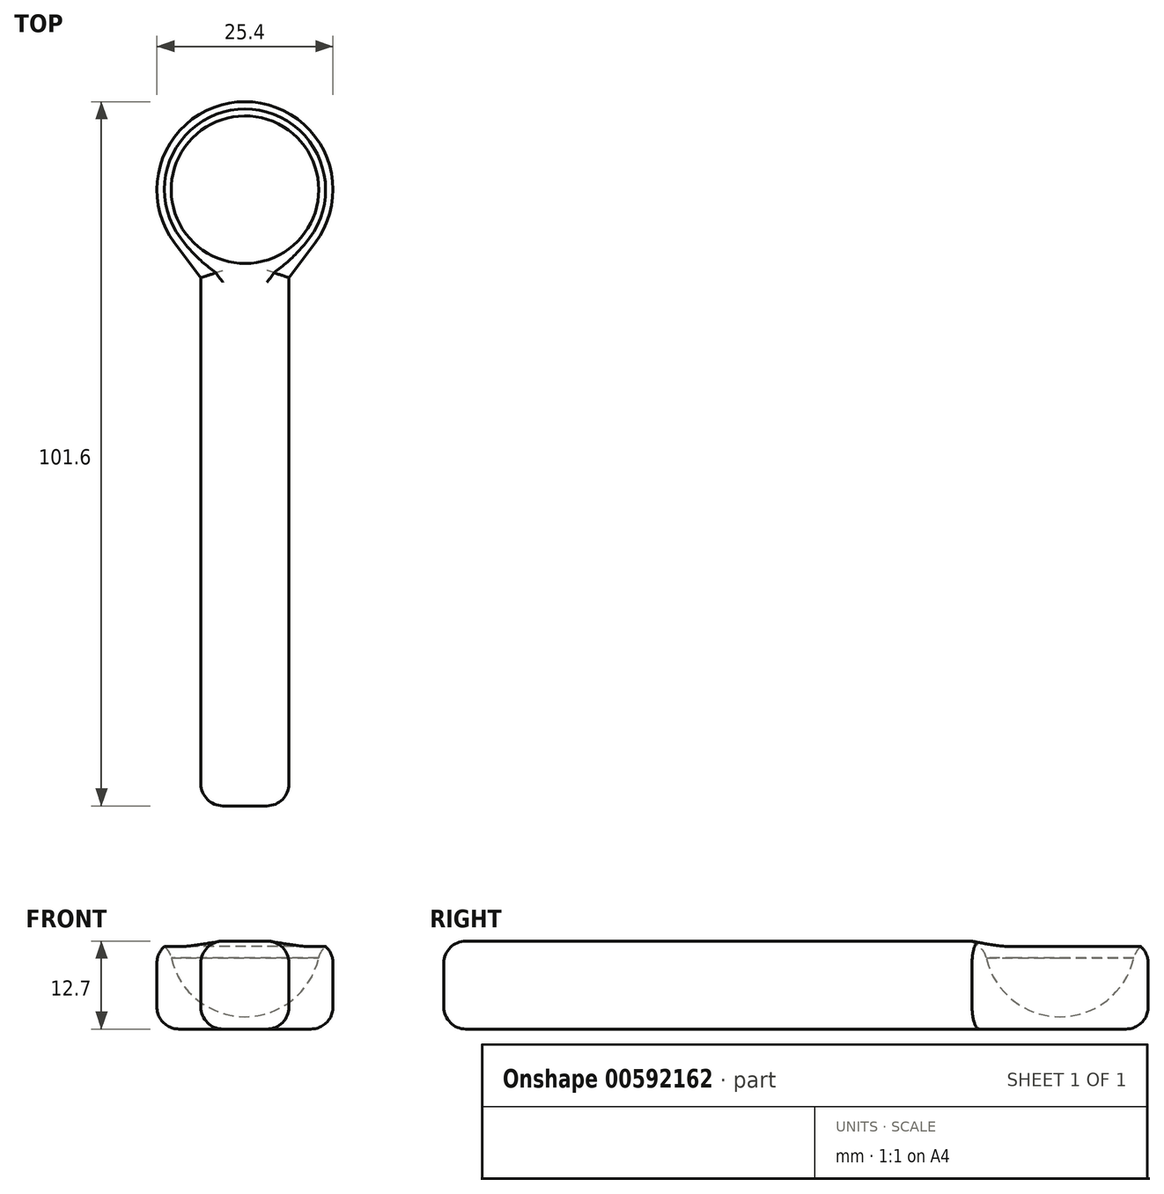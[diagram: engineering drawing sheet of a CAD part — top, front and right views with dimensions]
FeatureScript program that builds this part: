
annotation { "Feature Type Name" : "Feature", "Feature Type Description" : "" }
export const myFeature = defineFeature(function(context is Context, id is Id, definition is map)
    precondition{}
    {
        {
            var Q0;
            Q0=qCreatedBy(makeId("Front.planeOp"),FACE);
            var sketch = newSketch(context, id + "F0", { "sketchPlane" : qUnion([Q0])});
            skLineSegment(sketch, "E0.bottom", {"start": v(6.35, 6.35) * mm, "end": v(-6.35, 6.35) * mm});
            skLineSegment(sketch, "E0.top", {"start": v(6.35, -6.35) * mm, "end": v(-6.35, -6.35) * mm});
            skLineSegment(sketch, "E0.left", {"start": v(6.35, 6.35) * mm, "end": v(6.35, -6.35) * mm});
            skLineSegment(sketch, "E0.right", {"start": v(-6.35, 6.35) * mm, "end": v(-6.35, -6.35) * mm});
            skPoint(sketch, "E0.middle", {"position": v(0, 0) * mm});
            skSolve(sketch);
        }
        {
            var Q0;
            Q0 = qSketchRegion(id + "F0", true);
            extrude(context, id + "F1", {"entities" : qUnion([Q0]), "depth" : 76.2 * mm, "offsetDistance" : 25.4 * mm});
        }
        {
            var Q0;
            Q0=makeQuery(id+"F1.opExtrude","SWEPT_FACE",FACE,{"disambiguationData":[OSD([sQuery(id+"F0.wireOp",EDGE,"E0.bottom")])]});
            var sketch = newSketch(context, id + "F2", { "sketchPlane" : qUnion([Q0])});
            skCircle(sketch, "E1", {"center": v(0, 12.7) * mm, "radius": 12.7 * mm});
            skLineSegment(sketch, "E2", {"start": v(-6.35, 0) * mm, "end": v(-10.16, 5.08) * mm});
            skLineSegment(sketch, "E3", {"start": v(6.35, 0) * mm, "end": v(10.16, 5.08) * mm});
            skSolve(sketch);
        }
        {
            var Q0;
            {var subQ0=sQuery(id+"F2.wireOp",EDGE,"E1");var subQ1=makeQuery(id+"F2.imprint","INTERSECT",VERTEX,{"derivedFrom":[subQ0,sQuery(id+"F2.wireOp",EDGE,"E2")]});Q0=makeQuery(id+"F2.imprint","IMPRINT",FACE,{"disambiguationData":[TD([[makeQuery(id+"F2.imprint","IMPRINT",EDGE,{"disambiguationData":[TD([[subQ1,-1.0]])],"derivedFrom":subQ0}),1.0]])]});}
            var Q1;
            {var subQ0=sQuery(id+"F2.wireOp",EDGE,"E2");Q1=makeQuery(id+"F2.imprint","IMPRINT",FACE,{"disambiguationData":[TD([[makeQuery(id+"F2.imprint","IMPRINT",EDGE,{"derivedFrom":subQ0}),-1.0]])]});}
            var Q2;
            {var subQ0=sQuery(id+"F2.wireOp",EDGE,"E3");Q2=makeQuery(id+"F2.imprint","IMPRINT",FACE,{"disambiguationData":[TD([[makeQuery(id+"F2.imprint","IMPRINT",EDGE,{"derivedFrom":subQ0}),1.0]])]});}
            extrude(context, id + "F3", {"entities" : qUnion([Q0, Q1, Q2]), "operationType" : NewBodyOperationType.ADD, "oppositeDirection" : true, "depth" : 12.7 * mm, "offsetDistance" : 25.4 * mm});
        }
        {
            var Q0;
            {var subQ0=sQuery(id+"F2.wireOp",EDGE,"E1");var subQ1=makeQuery(id+"F2.imprint","INTERSECT",VERTEX,{"derivedFrom":[subQ0,sQuery(id+"F2.wireOp",EDGE,"E2")]});Q0=makeQuery(id+"F2.imprint","IMPRINT",FACE,{"disambiguationData":[TD([[makeQuery(id+"F2.imprint","IMPRINT",EDGE,{"disambiguationData":[TD([[subQ1,-1.0]])],"derivedFrom":subQ0}),1.0]])]});}
            var sketch = newSketch(context, id + "F4", { "sketchPlane" : qUnion([Q0])});
            skArc(sketch, "E4", {"start": v(0, 1.78) * mm, "mid": v(10.92, 12.7) * mm, "end": v(0, 23.62) * mm});
            skLineSegment(sketch, "E5", {"start": v(0, 23.62) * mm, "end": v(0, 1.78) * mm});
            skSolve(sketch);
        }
        {
            var Q0;
            Q0 = qSketchRegion(id + "F4", true);
            var Q1;
            Q1=sQuery(id+"F4.wireOp",EDGE,"E5");
            revolve(context, id + "F5", {"operationType" : NewBodyOperationType.REMOVE, "entities" : qUnion([Q0]), "axis" : qUnion([Q1]), "revolveType" : RevolveType.FULL, "oppositeDirection" : true});
        }
        {
            var Q0;
            {var subQ0=sQuery(id+"F0.wireOp",EDGE,"E0.bottom");Q0=makeQuery(id+"F3.boolean.opBoolean","MERGE",FACE,{"derivedFrom":[makeQuery(id+"F1.opExtrude","SWEPT_FACE",FACE,{"disambiguationData":[OSD([subQ0])]}),makeQuery(id+"F3.opExtrude","CAP_FACE",FACE,{"disambiguationData":[OSD([subQ0,sQuery(id+"F2.wireOp",EDGE,"E1"),sQuery(id+"F2.wireOp",EDGE,"E2"),sQuery(id+"F2.wireOp",EDGE,"E3")])],"isStart":true})]});}
            var Q1;
            Q1=makeQuery(id+"F3.boolean.opBoolean","MERGE",FACE,{"derivedFrom":[makeQuery(id+"F1.opExtrude","SWEPT_FACE",FACE,{"disambiguationData":[OSD([sQuery(id+"F0.wireOp",EDGE,"E0.top")])]}),makeQuery(id+"F3.opExtrude","CAP_FACE",FACE,{"disambiguationData":[OSD([sQuery(id+"F0.wireOp",EDGE,"E0.bottom"),sQuery(id+"F2.wireOp",EDGE,"E1"),sQuery(id+"F2.wireOp",EDGE,"E2"),sQuery(id+"F2.wireOp",EDGE,"E3")])],"isStart":false})]});
            var Q2;
            Q2=makeQuery(id+"F1.opExtrude","CAP_FACE",FACE,{"disambiguationData":[OSD([sQuery(id+"F0.wireOp",EDGE,"E0.bottom"),sQuery(id+"F0.wireOp",EDGE,"E0.top"),sQuery(id+"F0.wireOp",EDGE,"E0.left"),sQuery(id+"F0.wireOp",EDGE,"E0.right")])],"isStart":false});
            fillet(context, id + "F6", {"entities" : qUnion([Q0, Q1, Q2]), "radius" : 3.17 * mm, "tangentPropagation" : true, "allowEdgeOverflow" : false});
        }
    });
